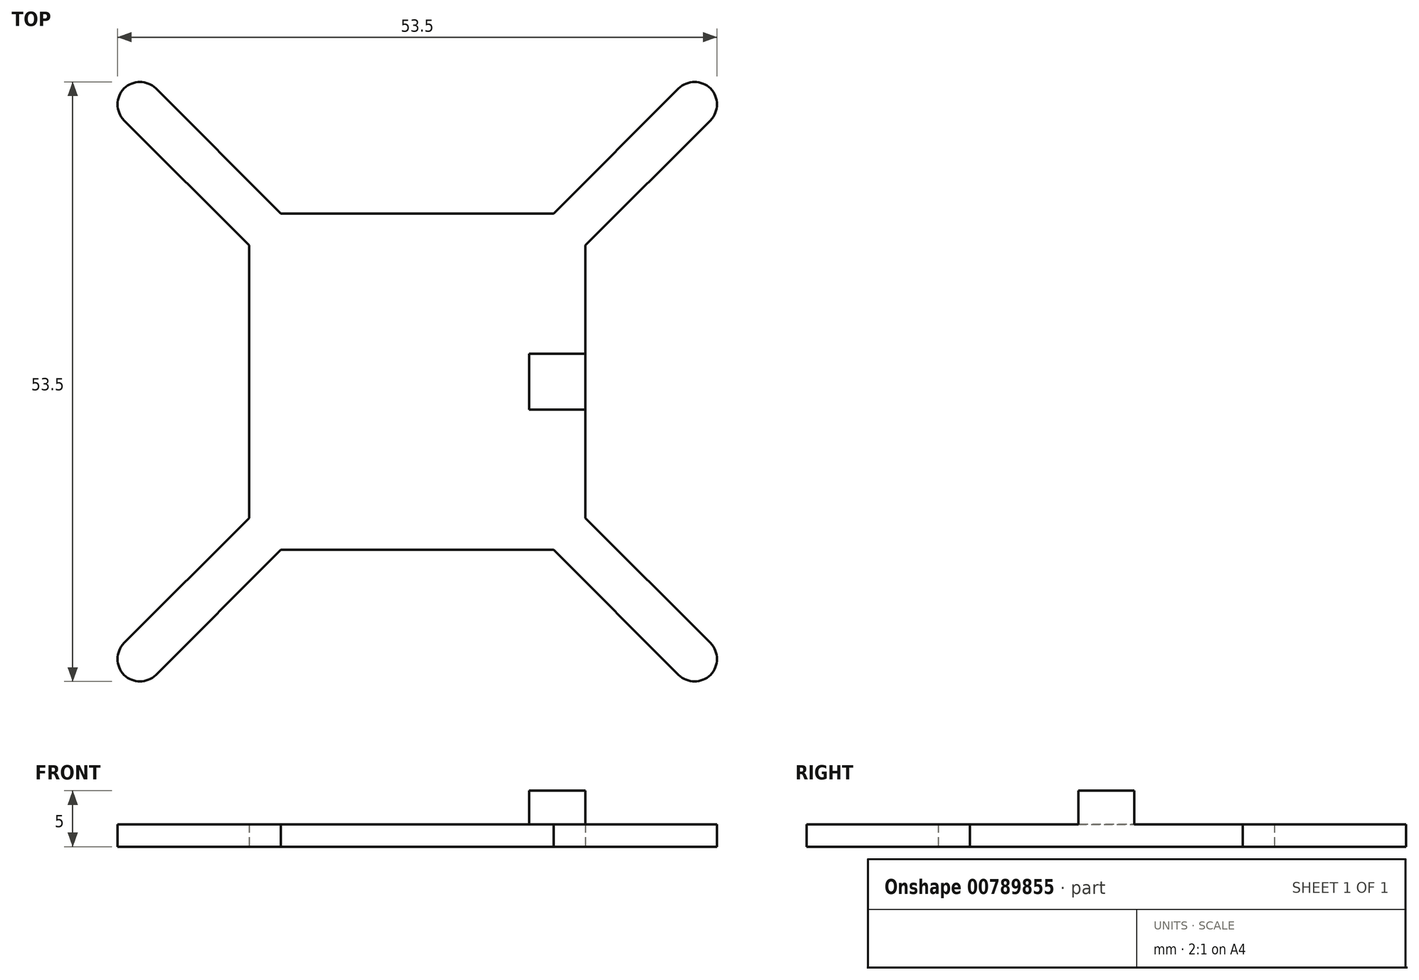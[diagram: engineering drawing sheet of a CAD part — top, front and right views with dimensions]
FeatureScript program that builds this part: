
annotation { "Feature Type Name" : "Feature", "Feature Type Description" : "" }
export const myFeature = defineFeature(function(context is Context, id is Id, definition is map)
    precondition{}
    {
        {
            var Q0;
            Q0=qCreatedBy(makeId("Top.planeOp"),FACE);
            var sketch = newSketch(context, id + "F0", { "sketchPlane" : qUnion([Q0])});
            skLineSegment(sketch, "E0.bottom", {"start": v(-12.17, 15) * mm, "end": v(12.17, 15) * mm});
            skLineSegment(sketch, "E0.top", {"start": v(-12.17, -15) * mm, "end": v(12.17, -15) * mm});
            skLineSegment(sketch, "E0.left", {"start": v(-15, 12.17) * mm, "end": v(-15, -12.17) * mm});
            skLineSegment(sketch, "E0.right", {"start": v(15, 12.17) * mm, "end": v(15, -12.17) * mm});
            skPoint(sketch, "E0.middle", {"position": v(0, 0) * mm});
            skLineSegment(sketch, "E1", {"start": v(-15, 12.17) * mm, "end": v(-26.16, 23.33) * mm});
            skLineSegment(sketch, "E2", {"start": v(-12.17, 15) * mm, "end": v(-23.33, 26.16) * mm});
            skArc(sketch, "E3", {"start": v(-23.33, 26.16) * mm, "mid": v(-26.16, 26.16) * mm, "end": v(-26.16, 23.33) * mm});
            skLineSegment(sketch, "E4", {"start": v(-24.75, 24.75) * mm, "end": v(0, 0) * mm, "construction": true});
            skLineSegment(sketch, "E5", {"start": v(-26.16, 23.33) * mm, "end": v(-23.33, 26.16) * mm, "construction": true});
            skLineSegment(sketch, "E6.1.0", {"start": v(-15, -12.17) * mm, "end": v(-26.16, -23.33) * mm});
            skLineSegment(sketch, "E6.1.1", {"start": v(-12.17, -15) * mm, "end": v(-23.33, -26.16) * mm});
            skArc(sketch, "E6.1.2", {"start": v(-26.16, -23.33) * mm, "mid": v(-26.16, -26.16) * mm, "end": v(-23.33, -26.16) * mm});
            skLineSegment(sketch, "E6.1.3", {"start": v(-23.33, -26.16) * mm, "end": v(-26.16, -23.33) * mm, "construction": true});
            skLineSegment(sketch, "E6.2.0", {"start": v(12.17, -15) * mm, "end": v(23.33, -26.16) * mm});
            skLineSegment(sketch, "E6.2.1", {"start": v(15, -12.17) * mm, "end": v(26.16, -23.33) * mm});
            skArc(sketch, "E6.2.2", {"start": v(23.33, -26.16) * mm, "mid": v(26.16, -26.16) * mm, "end": v(26.16, -23.33) * mm});
            skLineSegment(sketch, "E6.2.3", {"start": v(26.16, -23.33) * mm, "end": v(23.33, -26.16) * mm, "construction": true});
            skLineSegment(sketch, "E6.3.0", {"start": v(15, 12.17) * mm, "end": v(26.16, 23.33) * mm});
            skLineSegment(sketch, "E6.3.1", {"start": v(12.17, 15) * mm, "end": v(23.33, 26.16) * mm});
            skArc(sketch, "E6.3.2", {"start": v(26.16, 23.33) * mm, "mid": v(26.16, 26.16) * mm, "end": v(23.33, 26.16) * mm});
            skLineSegment(sketch, "E6.3.3", {"start": v(23.33, 26.16) * mm, "end": v(26.16, 23.33) * mm, "construction": true});
            skSolve(sketch);
        }
        {
            var Q0;
            Q0=makeQuery(id+"F0.imprint","IMPRINT",FACE,{"disambiguationData":[TD([[makeQuery(id+"F0.imprint","IMPRINT",EDGE,{"derivedFrom":sQuery(id+"F0.wireOp",EDGE,"E0.bottom")}),-1.0]])]});
            extrude(context, id + "F1", {"entities" : qUnion([Q0]), "depth" : 2 * mm, "offsetDistance" : 25 * mm});
        }
        {
            var Q0;
            Q0=makeQuery(id+"F1.opExtrude","CAP_FACE",FACE,{"disambiguationData":[OSD([sQuery(id+"F0.wireOp",EDGE,"E0.bottom"),sQuery(id+"F0.wireOp",EDGE,"E0.top"),sQuery(id+"F0.wireOp",EDGE,"E0.left"),sQuery(id+"F0.wireOp",EDGE,"E0.right"),sQuery(id+"F0.wireOp",EDGE,"E1"),sQuery(id+"F0.wireOp",EDGE,"E2"),sQuery(id+"F0.wireOp",EDGE,"E3"),sQuery(id+"F0.wireOp",EDGE,"E6.1.0"),sQuery(id+"F0.wireOp",EDGE,"E6.1.1"),sQuery(id+"F0.wireOp",EDGE,"E6.1.2"),sQuery(id+"F0.wireOp",EDGE,"E6.2.0"),sQuery(id+"F0.wireOp",EDGE,"E6.2.1"),sQuery(id+"F0.wireOp",EDGE,"E6.2.2"),sQuery(id+"F0.wireOp",EDGE,"E6.3.0"),sQuery(id+"F0.wireOp",EDGE,"E6.3.1"),sQuery(id+"F0.wireOp",EDGE,"E6.3.2")])],"isStart":false});
            var sketch = newSketch(context, id + "F2", { "sketchPlane" : qUnion([Q0])});
            skLineSegment(sketch, "E7.bottom", {"start": v(15, -2.5) * mm, "end": v(10, -2.5) * mm});
            skLineSegment(sketch, "E7.top", {"start": v(15, 2.5) * mm, "end": v(10, 2.5) * mm});
            skLineSegment(sketch, "E7.left", {"start": v(15, -2.5) * mm, "end": v(15, 2.5) * mm});
            skLineSegment(sketch, "E7.right", {"start": v(10, -2.5) * mm, "end": v(10, 2.5) * mm});
            skLineSegment(sketch, "E8", {"start": v(10, 0) * mm, "end": v(15, 0) * mm, "construction": true});
            skSolve(sketch);
        }
        {
            var Q0;
            Q0=makeQuery(id+"F2.imprint","IMPRINT",FACE,{"disambiguationData":[TD([[makeQuery(id+"F2.imprint","IMPRINT",EDGE,{"derivedFrom":sQuery(id+"F2.wireOp",EDGE,"E7.bottom")}),-1.0]])]});
            extrude(context, id + "F3", {"entities" : qUnion([Q0]), "operationType" : NewBodyOperationType.ADD, "depth" : 3 * mm, "offsetDistance" : 25 * mm});
        }
    });
